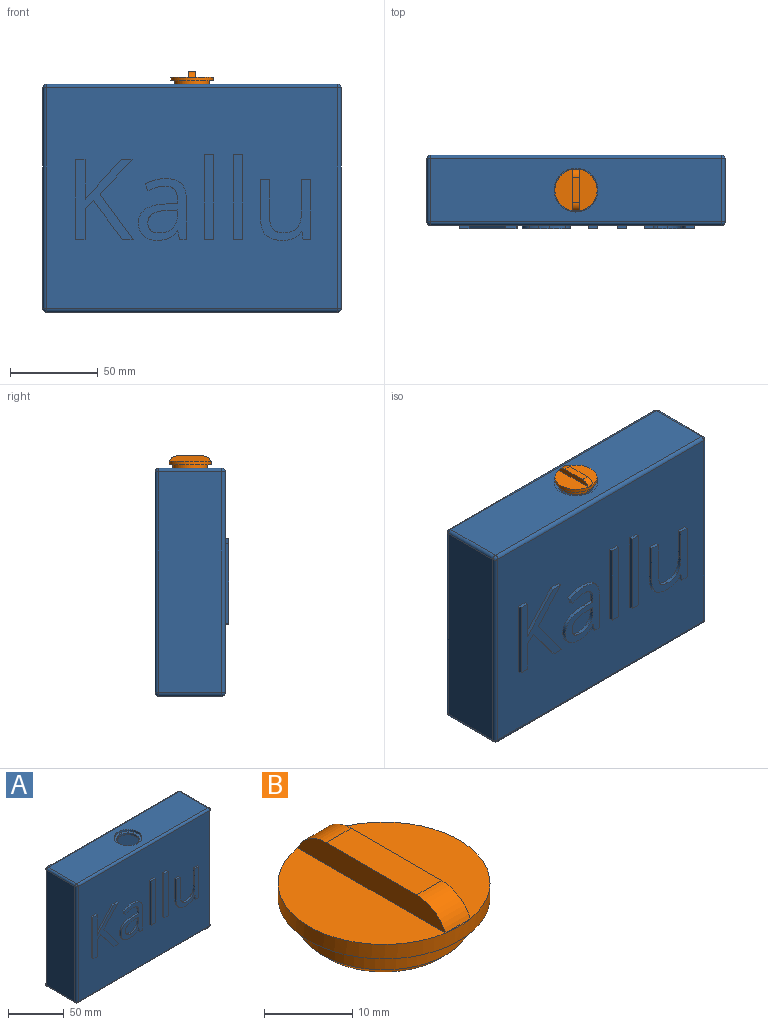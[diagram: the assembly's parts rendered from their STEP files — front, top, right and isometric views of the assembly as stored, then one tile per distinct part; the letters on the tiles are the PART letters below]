
ASSEMBLY  parts=2 mates=1
PART A: 111 faces, bbox 170x42x130 mm
  f0: plane 166x1mm, normal (0,0,-1), area 165.8mm2, adj f3,f4,f8,f109
  f1: plane 166x1mm, normal (0,0,-1), area 165.8mm2, adj f3,f4,f7,f107
  f2: plane 166x22.01mm, normal (0,0,-1), area 3339.2mm2, adj f3,f4,f9,f108,f110
  f3: plane 124x36mm, normal (1,0,0), area 4428.3mm2, adj f0,f1,f2,f6,f7,f8,f107,f108
  f4: plane 124x36mm, normal (-1,0,0), area 4428.3mm2, adj f0,f1,f2,f6,f7,f8,f107,f108
  f5: plane 166x126mm, normal (0,-1,0), area 18821.7mm2, adj f22,f31,f32,f36,f37,f38,f39,f40
  f6: plane 166x36mm, normal (0,0,1), area 5976mm2, adj f3,f4,f7,f8
  f7: plane 166x124mm, normal (0,-1,0), area 20584mm2, adj f1,f3,f4,f6
  f8: plane 166x124mm, normal (0,1,0), area 20584mm2, adj f0,f3,f4,f6
  f9: cylinder r=10mm len=20mm, axis (0,0,1), area 125.7mm2, adj f2,f16
  f10: plane 126x36mm, normal (-1,0,0), area 4536mm2, adj f25,f30,f33,f36
  f11: plane 126x36mm, normal (1,0,0), area 4536mm2, adj f17,f21,f22,f23
  f12: plane 166x126mm, normal (0,1,0), area 20916mm2, adj f17,f20,f24,f25
  f13: plane 166x36mm, normal (0,0,1), area 5485.1mm2, adj f15,f20,f21,f30,f31
  f14: plane 166x36mm, normal (0,0,-1), area 5976mm2, adj f23,f24,f32,f33
  f15: cylinder r=12.5mm len=25mm, axis (0,0,1), area 157.1mm2, adj f13,f16
  f16: plane 25x25mm, normal (0,0,1), area 176.7mm2, adj f9,f15
  f17: cylinder r=2mm len=126mm, axis (0,0,1), area 395.8mm2, adj f11,f12,f18,f19
  f18: sphere r=2mm, area 6.3mm2, adj f17,f20,f21
  f19: sphere r=2mm, area 6.3mm2, adj f17,f23,f24
  f20: cylinder r=2mm len=166mm, axis (1,0,0), area 521.5mm2, adj f12,f13,f18,f26
  f21: cylinder r=2mm len=36mm, axis (0,-1,0), area 113.1mm2, adj f11,f13,f18,f27
  f22: cylinder r=2mm len=126mm, axis (0,0,-1), area 395.8mm2, adj f5,f11,f27,f28
  f23: cylinder r=2mm len=36mm, axis (0,1,0), area 113.1mm2, adj f11,f14,f19,f28
  f24: cylinder r=2mm len=166mm, axis (-1,0,0), area 521.5mm2, adj f12,f14,f19,f29
  f25: cylinder r=2mm len=126mm, axis (0,0,-1), area 395.8mm2, adj f10,f12,f26,f29
  f26: sphere r=2mm, area 6.3mm2, adj f20,f25,f30
  f27: sphere r=2mm, area 6.3mm2, adj f21,f22,f31
  f28: sphere r=2mm, area 6.3mm2, adj f22,f23,f32
  f29: sphere r=2mm, area 6.3mm2, adj f24,f25,f33
  f30: cylinder r=2mm len=36mm, axis (0,1,0), area 113.1mm2, adj f10,f13,f26,f34
  f31: cylinder r=2mm len=166mm, axis (-1,0,0), area 521.5mm2, adj f5,f13,f27,f34
  f32: cylinder r=2mm len=166mm, axis (1,0,0), area 521.5mm2, adj f5,f14,f28,f35
  f33: cylinder r=2mm len=36mm, axis (0,-1,0), area 113.1mm2, adj f10,f14,f29,f35
  f34: sphere r=2mm, area 6.3mm2, adj f30,f31,f36
  f35: sphere r=2mm, area 6.3mm2, adj f32,f33,f36
  f36: cylinder r=2mm len=126mm, axis (0,0,1), area 395.8mm2, adj f5,f10,f34,f35
  f37: plane 6.21x2mm, normal (0,0,-1), area 12.4mm2, adj f5,f38,f48,f49
  f38: plane 25.68x18.94mm, normal (0.8,0,0.59), area 63.8mm2, adj f5,f37,f39,f49
  f39: plane 19.73x18.26mm, normal (0.73,0,-0.68), area 53.8mm2, adj f5,f38,f40,f49
  f40: plane 6.24x2mm, normal (0,0,1), area 12.5mm2, adj f5,f39,f41,f49
  f41: plane 22.52x20.59mm, normal (-0.74,0,0.67), area 61mm2, adj f5,f40,f42,f49
  f42: plane 22.52x2mm, normal (1,0,0), area 45mm2, adj f5,f41,f43,f49
  f43: plane 5.28x2mm, normal (0,0,1), area 10.6mm2, adj f5,f42,f44,f49
  f44: plane 45.41x2mm, normal (-1,0,0), area 90.8mm2, adj f5,f43,f45,f49
  f45: plane 5.28x2mm, normal (0,0,-1), area 10.6mm2, adj f5,f44,f46,f49
  f46: plane 17.8x2mm, normal (1,0,0), area 35.6mm2, adj f5,f45,f47,f49
  f47: plane 4.76x4.22mm, normal (0.66,0,-0.75), area 12.7mm2, adj f5,f46,f48,f49
  f48: plane 22.02x16.55mm, normal (-0.8,0,-0.6), area 55.1mm2, adj f5,f37,f47,f49
  f49: plane 45.41x32.79mm, normal (0,-1,0), area 543.5mm2, adj f37,f38,f39,f40,f41,f42,f43,f44
  f50: extruded ~7.57x2.64mm, area 16.4mm2, adj f51,f76,f77,f78
  f51: extruded ~4.73x2mm, area 10.1mm2, adj f50,f52,f77,f78
  f52: extruded ~4.26x2mm, area 9.5mm2, adj f51,f53,f77,f78
  f53: extruded ~5.26x2.71mm, area 12.4mm2, adj f52,f54,f77,f78
  f54: extruded ~8.86x2mm, area 18.3mm2, adj f53,f55,f77,f78
  f55: plane 5.16x2mm, normal (0.04,0,-1), area 10.3mm2, adj f54,f56,f77,f78
  f56: plane 3.07x2mm, normal (-1,0,0), area 6.1mm2, adj f55,f76,f77,f78
  f57: plane 4.85x2mm, normal (-0.98,0,-0.21), area 9.9mm2, adj f5,f58,f75,f77
  f58: plane 3.83x2mm, normal (0,0,-1), area 7.7mm2, adj f5,f57,f59,f77
  f59: plane 23.23x2mm, normal (1,0,0), area 46.5mm2, adj f5,f58,f60,f77
  f60: extruded ~8.66x2.94mm, area 18.8mm2, adj f5,f59,f61,f77
  f61: extruded ~9.02x2.7mm, area 19.3mm2, adj f5,f60,f62,f77
  f62: extruded ~6.02x2mm, area 12.2mm2, adj f5,f61,f63,f77
  f63: extruded ~5.51x2.14mm, area 11.8mm2, adj f5,f62,f64,f77
  f64: plane 3.95x2mm, normal (-0.93,0,-0.37), area 8.5mm2, adj f5,f63,f65,f77
  f65: extruded ~9.62x2.6mm, area 20.1mm2, adj f5,f64,f66,f77
  f66: extruded ~5.52x2mm, area 12mm2, adj f5,f65,f67,f77
  f67: extruded ~5.91x2mm, area 12.6mm2, adj f5,f66,f68,f77
  f68: plane 2.12x2mm, normal (-1,0,0), area 4.2mm2, adj f5,f67,f69,f77
  f69: plane 5.77x2mm, normal (-0.03,0,1), area 11.6mm2, adj f5,f68,f70,f77
  f70: extruded ~16.49x10.8mm, area 44.3mm2, adj f5,f69,f71,f77
  f71: extruded ~7.42x2.87mm, area 16.4mm2, adj f5,f70,f72,f77
  f72: extruded ~7.93x2.61mm, area 17.1mm2, adj f5,f71,f73,f77
  f73: extruded ~6.33x2mm, area 12.9mm2, adj f5,f72,f74,f77
  f74: extruded ~5.07x4.34mm, area 13.5mm2, adj f5,f73,f75,f77
  f75: plane 2x0.25mm, normal (0,0,-1), area 0.5mm2, adj f5,f57,f74,f77
  f76: extruded ~7.39x2.75mm, area 16.2mm2, adj f50,f56,f77,f78
  f77: plane 35.22x27.3mm, normal (0,-1,0), area 453.9mm2, adj f50,f51,f52,f53,f54,f55,f56,f57
  f78: plane 16.74x13.1mm, normal (0,-1,0), area 176.7mm2, adj f50,f51,f52,f53,f54,f55,f56,f76
  f79: plane 5.16x2mm, normal (0,0,-1), area 10.3mm2, adj f5,f80,f82,f83
  f80: plane 48.33x2mm, normal (1,0,0), area 96.7mm2, adj f5,f79,f81,f83
  f81: plane 5.16x2mm, normal (0,0,1), area 10.3mm2, adj f5,f80,f82,f83
  f82: plane 48.33x2mm, normal (-1,0,0), area 96.7mm2, adj f5,f79,f81,f83
  f83: plane 48.33x5.16mm, normal (0,-1,0), area 249.3mm2, adj f79,f80,f81,f82
  f84: plane 5.16x2mm, normal (0,0,-1), area 10.3mm2, adj f5,f85,f87,f88
  f85: plane 48.33x2mm, normal (1,0,0), area 96.7mm2, adj f5,f84,f86,f88
  f86: plane 5.16x2mm, normal (0,0,1), area 10.3mm2, adj f5,f85,f87,f88
  f87: plane 48.33x2mm, normal (-1,0,0), area 96.7mm2, adj f5,f84,f86,f88
  f88: plane 48.33x5.16mm, normal (0,-1,0), area 249.3mm2, adj f84,f85,f86,f87
  f89: plane 22.08x2mm, normal (1,0,0), area 44.2mm2, adj f5,f90,f105,f106
  f90: plane 5.22x2mm, normal (0,0,1), area 10.4mm2, adj f5,f89,f91,f106
  f91: plane 22.27x2mm, normal (-1,0,0), area 44.5mm2, adj f5,f90,f92,f106
  f92: extruded ~9.44x3.09mm, area 20.4mm2, adj f5,f91,f93,f106
  f93: extruded ~9.3x2.95mm, area 20mm2, adj f5,f92,f94,f106
  f94: extruded ~6.42x2mm, area 13.2mm2, adj f5,f93,f95,f106
  f95: extruded ~4.39x3.85mm, area 11.8mm2, adj f5,f94,f96,f106
  f96: plane 2x0.28mm, normal (0,0,-1), area 0.6mm2, adj f5,f95,f97,f106
  f97: plane 4.56x2mm, normal (-0.99,0,-0.16), area 9.2mm2, adj f5,f96,f98,f106
  f98: plane 4.25x2mm, normal (0,0,-1), area 8.5mm2, adj f5,f97,f99,f106
  f99: plane 34.04x2mm, normal (1,0,0), area 68.1mm2, adj f5,f98,f100,f106
  f100: plane 5.16x2mm, normal (0,0,1), area 10.3mm2, adj f5,f99,f101,f106
  f101: plane 17.89x2mm, normal (-1,0,0), area 35.8mm2, adj f5,f100,f102,f106
  f102: extruded ~9.54x2.46mm, area 20.1mm2, adj f5,f101,f103,f106
  f103: extruded ~7.81x2.92mm, area 17.2mm2, adj f5,f102,f104,f106
  f104: extruded ~5.93x2.05mm, area 12.9mm2, adj f5,f103,f105,f106
  f105: extruded ~6.21x2mm, area 13.3mm2, adj f5,f89,f104,f106
  f106: plane 34.66x28.47mm, normal (0,-1,0), area 421.8mm2, adj f89,f90,f91,f92,f93,f94,f95,f96
  f107: plane 166x5.95mm, normal (0,1,0), area 986.9mm2, adj f1,f3,f4,f108
  f108: plane 166x6mm, normal (0,-0.7,-0.71), area 1401.7mm2, adj f2,f3,f4,f107
  f109: plane 166x5.95mm, normal (0,-1,0), area 986.9mm2, adj f0,f3,f4,f110
  f110: plane 166x6mm, normal (0,0.7,-0.71), area 1401.7mm2, adj f2,f3,f4,f109
PART B: 14 faces, bbox 24x24x9 mm
  f0: plane 4x0.17mm, normal (0,0,1), area 0.4mm2, adj f6,f13
  f1: plane 23.66x10mm, normal (0,0,1), area 178.4mm2, adj f6,f10
  f2: plane 4x0.17mm, normal (0,0,1), area 0.4mm2, adj f6,f12
  f3: cylinder r=9.9mm len=19.8mm, axis (0,0,-1), area 186.6mm2, adj f5,f8
  f4: plane 17.8x17.8mm, normal (0,0,-1), area 248.8mm2, adj f5
  f5: cone r=9.9mm half-angle=45deg, axis (0,0,1), area 83.5mm2, adj f3,f4
  f6: cylinder r=12mm len=24mm, axis (0,0,-1), area 150.8mm2, adj f0,f1,f2,f7,f8
  f7: plane 23.66x10mm, normal (0,0,1), area 178.4mm2, adj f6,f9
  f8: plane 24x24mm, normal (0,0,-1), area 144.5mm2, adj f3,f6
  f9: plane 23.66x3mm, normal (-1,0,0), area 63.3mm2, adj f7,f11,f12,f13
  f10: plane 23.66x3mm, normal (1,0,0), area 63.3mm2, adj f1,f11,f12,f13
  f11: plane 14.5x4mm, normal (0,0,1), area 58mm2, adj f9,f10,f12,f13
  f12: cylinder r=5mm len=4.58mm, axis (1,0,0), area 23.2mm2, adj f2,f9,f10,f11
  f13: cylinder r=5mm len=4.58mm, axis (1,0,0), area 23.2mm2, adj f0,f9,f10,f11
PLACE A at identity
PLACE B t=(13.77,27.7,128)mm
MATE slider B.f3 <-> A.f9  axis (0,0,-1) through (13.77,27.7,128)mm
